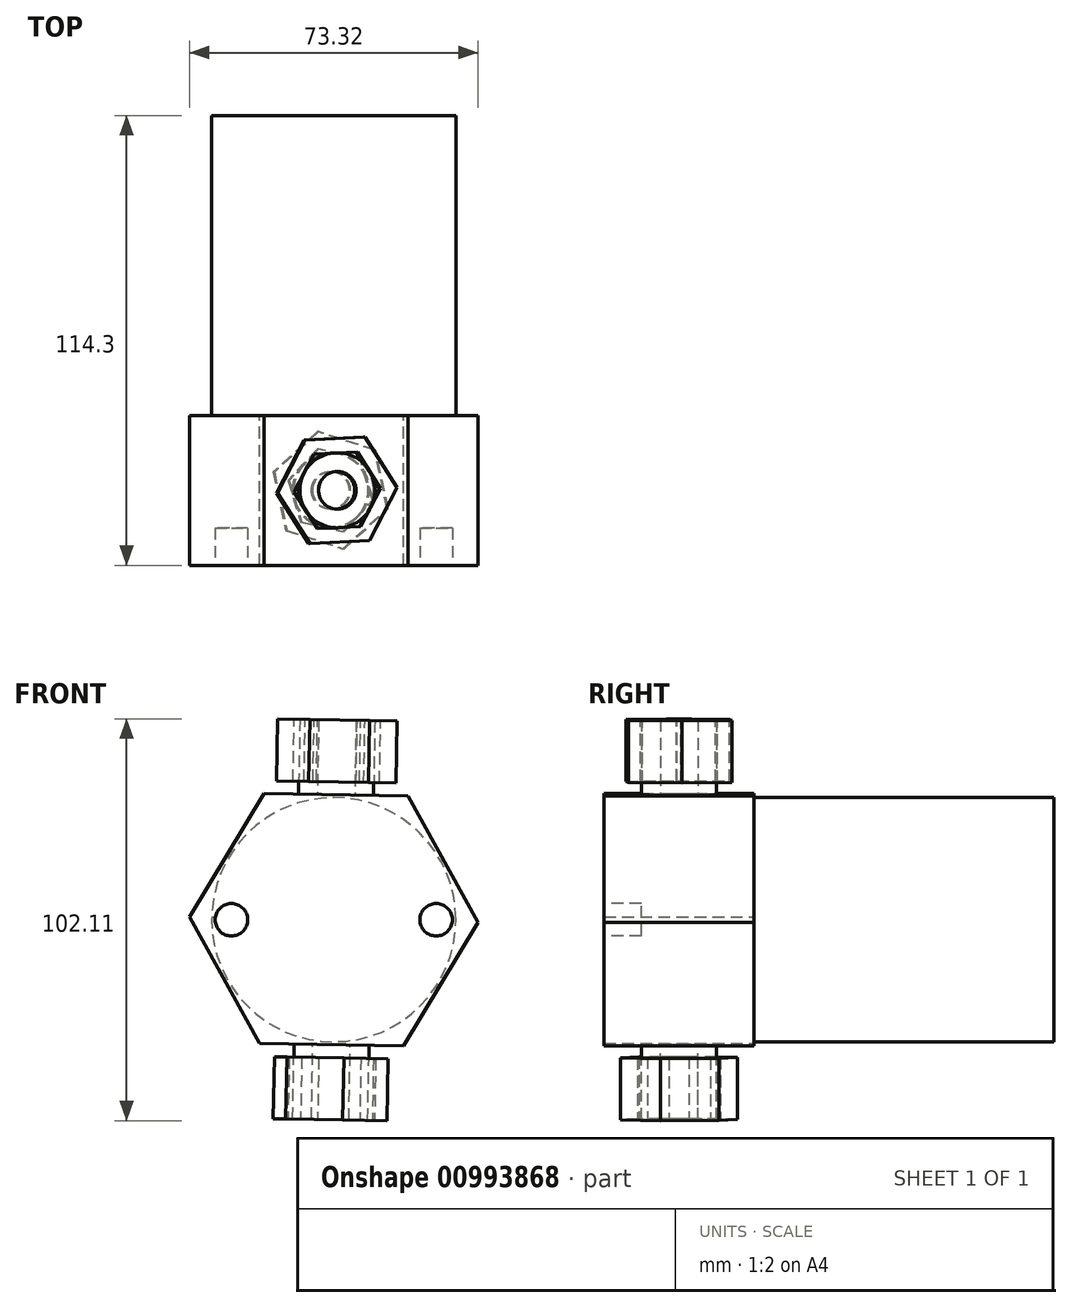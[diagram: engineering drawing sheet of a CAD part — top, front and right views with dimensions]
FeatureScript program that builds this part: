
annotation { "Feature Type Name" : "Feature", "Feature Type Description" : "" }
export const myFeature = defineFeature(function(context is Context, id is Id, definition is map)
    precondition{}
    {
        {
            var Q0;
            Q0=qCreatedBy(makeId("Front.planeOp"),FACE);
            var sketch = newSketch(context, id + "F0", { "sketchPlane" : qUnion([Q0])});
            skCircle(sketch, "E0.cCircle", {"center": v(0, 0) * mm, "radius": 31.75 * mm, "construction": true});
            skLineSegment(sketch, "E0.0", {"start": v(36.66, -0.66) * mm, "end": v(17.76, -32.07) * mm});
            skLineSegment(sketch, "E0.1", {"start": v(17.76, -32.07) * mm, "end": v(-18.9, -31.42) * mm});
            skLineSegment(sketch, "E0.2", {"start": v(-18.9, -31.42) * mm, "end": v(-36.66, 0.66) * mm});
            skLineSegment(sketch, "E0.3", {"start": v(-36.66, 0.66) * mm, "end": v(-17.76, 32.07) * mm});
            skLineSegment(sketch, "E0.4", {"start": v(-17.76, 32.07) * mm, "end": v(18.9, 31.42) * mm});
            skLineSegment(sketch, "E0.5", {"start": v(18.9, 31.42) * mm, "end": v(36.66, -0.66) * mm});
            skPoint(sketch, "E0.0.midPoint", {"position": v(27.2, -16.37) * mm});
            skSolve(sketch);
        }
        {
            var Q0;
            Q0 = qSketchRegion(id + "F0", true);
            extrude(context, id + "F1", {"entities" : qUnion([Q0]), "depth" : 38.1 * mm, "offsetDistance" : 25.4 * mm});
        }
        {
            var Q0;
            Q0=makeQuery(id+"F1.opExtrude","SWEPT_FACE",FACE,{"disambiguationData":[OSD([sQuery(id+"F0.wireOp",EDGE,"E0.1")])]});
            var sketch = newSketch(context, id + "F2", { "sketchPlane" : qUnion([Q0])});
            skCircle(sketch, "E1", {"center": v(0, 19.05) * mm, "radius": 9.53 * mm});
            skPoint(sketch, "E1.centerSnap0", {"position": v(18.33, 19.05) * mm});
            skPoint(sketch, "E1.centerSnap1", {"position": v(0, 38.1) * mm});
            skCircle(sketch, "E2", {"center": v(0, 19.05) * mm, "radius": 4.76 * mm});
            skSolve(sketch);
        }
        {
            var Q0;
            Q0 = qSketchRegion(id + "F2", true);
            extrude(context, id + "F3", {"entities" : qUnion([Q0]), "depth" : 19.05 * mm, "offsetDistance" : 25.4 * mm});
        }
        {
            var Q0;
            Q0=makeQuery(id+"F3.opExtrude","CAP_FACE",FACE,{"disambiguationData":[OSD([sQuery(id+"F2.wireOp",EDGE,"E1"),sQuery(id+"F2.wireOp",EDGE,"E2")])],"isStart":false});
            var sketch = newSketch(context, id + "F4", { "sketchPlane" : qUnion([Q0])});
            skCircle(sketch, "E3.cCircle", {"center": v(0, 19.05) * mm, "radius": 9.53 * mm, "construction": true});
            skLineSegment(sketch, "E3.0", {"start": v(10.7, 21.56) * mm, "end": v(7.53, 11.03) * mm});
            skLineSegment(sketch, "E3.1", {"start": v(7.53, 11.03) * mm, "end": v(-3.18, 8.52) * mm});
            skLineSegment(sketch, "E3.2", {"start": v(-3.18, 8.52) * mm, "end": v(-10.7, 16.54) * mm});
            skLineSegment(sketch, "E3.3", {"start": v(-10.7, 16.54) * mm, "end": v(-7.53, 27.07) * mm});
            skLineSegment(sketch, "E3.4", {"start": v(-7.53, 27.07) * mm, "end": v(3.18, 29.58) * mm});
            skLineSegment(sketch, "E3.5", {"start": v(3.18, 29.58) * mm, "end": v(10.7, 21.56) * mm});
            skPoint(sketch, "E3.0.midPoint", {"position": v(9.12, 16.3) * mm});
            skCircle(sketch, "E4.cCircle", {"center": v(0, 19.05) * mm, "radius": 13.17 * mm, "construction": true});
            skLineSegment(sketch, "E4.0", {"start": v(14.47, 23.73) * mm, "end": v(11.3, 8.86) * mm});
            skLineSegment(sketch, "E4.1", {"start": v(11.3, 8.86) * mm, "end": v(-3.18, 4.17) * mm});
            skLineSegment(sketch, "E4.2", {"start": v(-3.18, 4.17) * mm, "end": v(-14.47, 14.37) * mm});
            skLineSegment(sketch, "E4.3", {"start": v(-14.47, 14.37) * mm, "end": v(-11.3, 29.24) * mm});
            skLineSegment(sketch, "E4.4", {"start": v(-11.3, 29.24) * mm, "end": v(3.18, 33.93) * mm});
            skLineSegment(sketch, "E4.5", {"start": v(3.18, 33.93) * mm, "end": v(14.47, 23.73) * mm});
            skPoint(sketch, "E4.0.midPoint", {"position": v(12.88, 16.3) * mm});
            skSolve(sketch);
        }
        {
            var Q0;
            Q0 = qSketchRegion(id + "F4", true);
            extrude(context, id + "F5", {"entities" : qUnion([Q0]), "oppositeDirection" : true, "depth" : 15.75 * mm, "offsetDistance" : 25.4 * mm});
        }
        {
            var Q0;
            Q0=makeQuery(id+"F1.opExtrude","SWEPT_FACE",FACE,{"disambiguationData":[OSD([sQuery(id+"F0.wireOp",EDGE,"E0.4")])]});
            var sketch = newSketch(context, id + "F6", { "sketchPlane" : qUnion([Q0])});
            skCircle(sketch, "E5", {"center": v(0, -19.05) * mm, "radius": 9.53 * mm});
            skPoint(sketch, "E5.centerSnap0", {"position": v(-18.33, -19.05) * mm});
            skCircle(sketch, "E6", {"center": v(0, -19.05) * mm, "radius": 4.76 * mm});
            skSolve(sketch);
        }
        {
            var Q0;
            Q0 = qSketchRegion(id + "F6", true);
            extrude(context, id + "F7", {"entities" : qUnion([Q0]), "depth" : 19.05 * mm, "offsetDistance" : 25.4 * mm});
        }
        {
            var Q0;
            Q0=makeQuery(id+"F7.opExtrude","CAP_FACE",FACE,{"disambiguationData":[OSD([sQuery(id+"F6.wireOp",EDGE,"E5"),sQuery(id+"F6.wireOp",EDGE,"E6")])],"isStart":false});
            var sketch = newSketch(context, id + "F8", { "sketchPlane" : qUnion([Q0])});
            skCircle(sketch, "E7.cCircle", {"center": v(0, -19.05) * mm, "radius": 9.53 * mm, "construction": true});
            skLineSegment(sketch, "E7.0", {"start": v(10.99, -18.56) * mm, "end": v(5.92, -28.32) * mm});
            skLineSegment(sketch, "E7.1", {"start": v(5.92, -28.32) * mm, "end": v(-5.07, -28.81) * mm});
            skLineSegment(sketch, "E7.2", {"start": v(-5.07, -28.81) * mm, "end": v(-10.99, -19.54) * mm});
            skLineSegment(sketch, "E7.3", {"start": v(-10.99, -19.54) * mm, "end": v(-5.92, -9.78) * mm});
            skLineSegment(sketch, "E7.4", {"start": v(-5.92, -9.78) * mm, "end": v(5.07, -9.29) * mm});
            skLineSegment(sketch, "E7.5", {"start": v(5.07, -9.29) * mm, "end": v(10.99, -18.56) * mm});
            skPoint(sketch, "E7.0.midPoint", {"position": v(8.45, -23.44) * mm});
            skCircle(sketch, "E8.cCircle", {"center": v(0, -19.05) * mm, "radius": 13.15 * mm, "construction": true});
            skLineSegment(sketch, "E8.0", {"start": v(15.17, -18.37) * mm, "end": v(8.18, -31.84) * mm});
            skLineSegment(sketch, "E8.1", {"start": v(8.18, -31.84) * mm, "end": v(-7, -32.53) * mm});
            skLineSegment(sketch, "E8.2", {"start": v(-7, -32.53) * mm, "end": v(-15.17, -19.73) * mm});
            skLineSegment(sketch, "E8.3", {"start": v(-15.17, -19.73) * mm, "end": v(-8.18, -6.26) * mm});
            skLineSegment(sketch, "E8.4", {"start": v(-8.18, -6.26) * mm, "end": v(7, -5.57) * mm});
            skLineSegment(sketch, "E8.5", {"start": v(7, -5.57) * mm, "end": v(15.17, -18.37) * mm});
            skPoint(sketch, "E8.0.midPoint", {"position": v(11.67, -25.1) * mm});
            skSolve(sketch);
        }
        {
            var Q0;
            Q0 = qSketchRegion(id + "F8", true);
            extrude(context, id + "F9", {"entities" : qUnion([Q0]), "oppositeDirection" : true, "depth" : 15.75 * mm, "offsetDistance" : 25.4 * mm});
        }
        {
            var Q0;
            Q0=makeQuery(id+"F1.opExtrude","CAP_FACE",FACE,{"disambiguationData":[OSD([sQuery(id+"F0.wireOp",EDGE,"E0.0"),sQuery(id+"F0.wireOp",EDGE,"E0.1"),sQuery(id+"F0.wireOp",EDGE,"E0.2"),sQuery(id+"F0.wireOp",EDGE,"E0.3"),sQuery(id+"F0.wireOp",EDGE,"E0.4"),sQuery(id+"F0.wireOp",EDGE,"E0.5")])],"isStart":true});
            var sketch = newSketch(context, id + "F10", { "sketchPlane" : qUnion([Q0])});
            skCircle(sketch, "E9", {"center": v(0, 0) * mm, "radius": 31.02 * mm});
            skSolve(sketch);
        }
        {
            var Q0;
            Q0 = qSketchRegion(id + "F10", true);
            extrude(context, id + "F11", {"entities" : qUnion([Q0]), "depth" : 76.2 * mm, "offsetDistance" : 25.4 * mm});
        }
        {
            var Q0;
            Q0=makeQuery(id+"F1.opExtrude","CAP_FACE",FACE,{"disambiguationData":[OSD([sQuery(id+"F0.wireOp",EDGE,"E0.0"),sQuery(id+"F0.wireOp",EDGE,"E0.1"),sQuery(id+"F0.wireOp",EDGE,"E0.2"),sQuery(id+"F0.wireOp",EDGE,"E0.3"),sQuery(id+"F0.wireOp",EDGE,"E0.4"),sQuery(id+"F0.wireOp",EDGE,"E0.5")])],"isStart":false});
            var sketch = newSketch(context, id + "F12", { "sketchPlane" : qUnion([Q0])});
            skLineSegment(sketch, "E10", {"start": v(0, 15.82) * mm, "end": v(0, -16.02) * mm, "construction": true});
            skCircle(sketch, "E11", {"center": v(-26.01, 0) * mm, "radius": 4.13 * mm});
            skCircle(sketch, "E12.MirrorC", {"center": v(26.01, 0) * mm, "radius": 4.13 * mm});
            skSolve(sketch);
        }
        {
            var Q0;
            Q0 = qSketchRegion(id + "F12", true);
            extrude(context, id + "F13", {"entities" : qUnion([Q0]), "operationType" : NewBodyOperationType.REMOVE, "oppositeDirection" : true, "depth" : 9.52 * mm, "offsetDistance" : 25.4 * mm});
        }
    });
